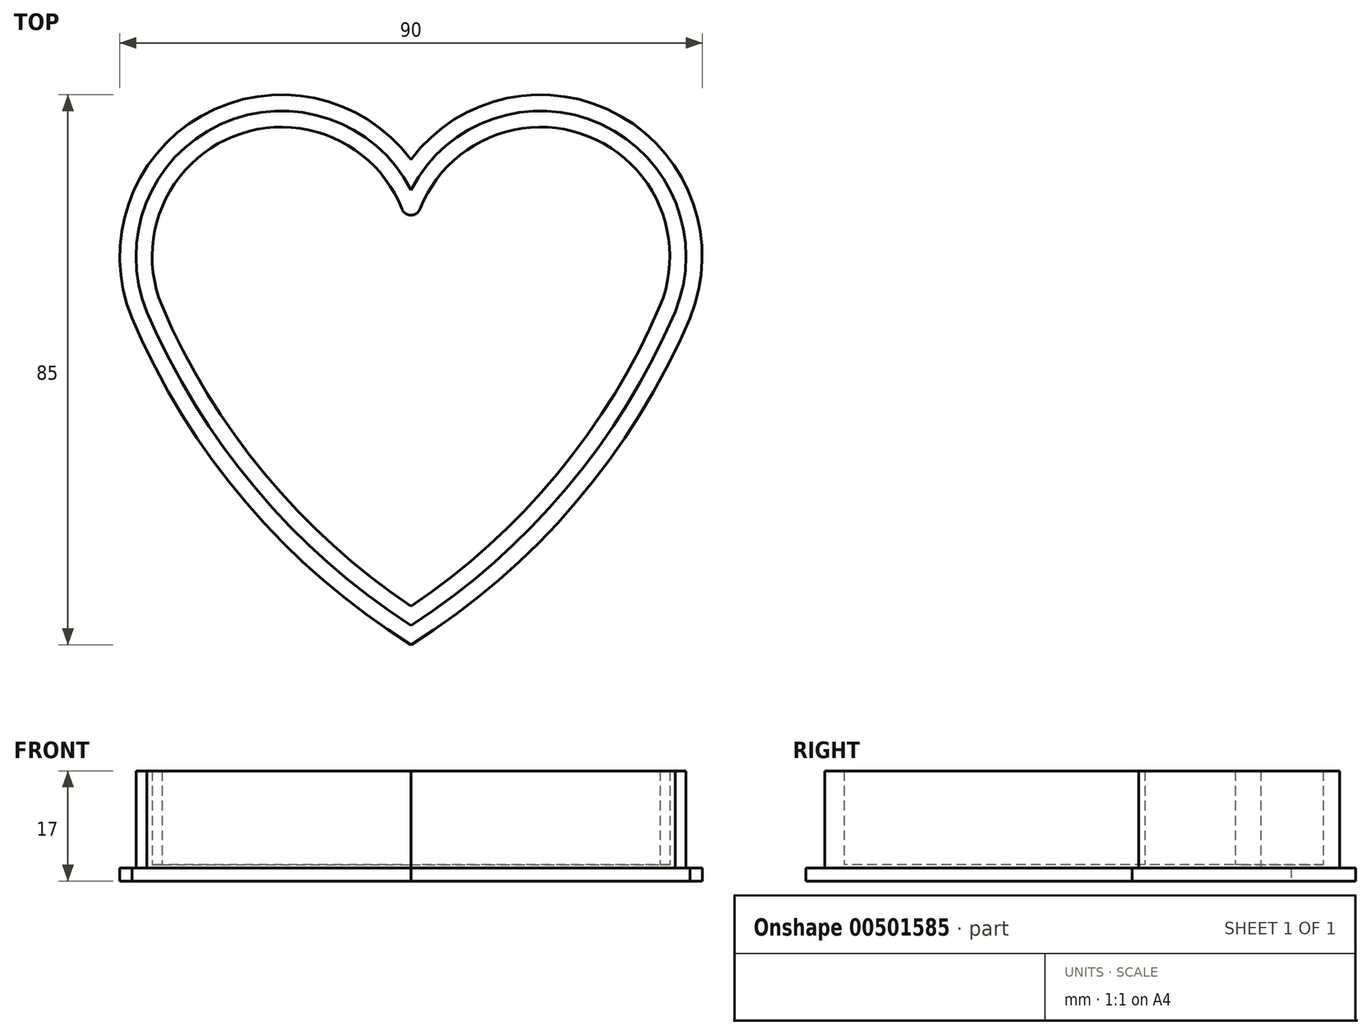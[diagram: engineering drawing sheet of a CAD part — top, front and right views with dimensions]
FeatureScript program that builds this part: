
annotation { "Feature Type Name" : "Feature", "Feature Type Description" : "" }
export const myFeature = defineFeature(function(context is Context, id is Id, definition is map)
    precondition{}
    {
        {
            var Q0;
            Q0=qCreatedBy(makeId("Top.planeOp"),FACE);
            var sketch = newSketch(context, id + "F0", { "sketchPlane" : qUnion([Q0])});
            skArc(sketch, "E0", {"start": v(-43.12, 5.48) * mm, "mid": v(-25.44, -23.07) * mm, "end": v(0, -45) * mm});
            skArc(sketch, "E1", {"start": v(0, 30) * mm, "mid": v(-32.36, 36.73) * mm, "end": v(-43.12, 5.48) * mm});
            skArc(sketch, "E2.MirrorCS", {"start": v(0, 30) * mm, "mid": v(32.36, 36.73) * mm, "end": v(43.12, 5.48) * mm});
            skArc(sketch, "E3.MirrorCS", {"start": v(43.12, 5.48) * mm, "mid": v(25.44, -23.07) * mm, "end": v(0, -45) * mm});
            skPoint(sketch, "E4.orphan", {"position": v(-1.9, 32.24) * mm});
            skPoint(sketch, "E5.orphan", {"position": v(1.9, 32.24) * mm});
            skSolve(sketch);
        }
        {
            var Q0;
            Q0=qSketchRegion(id+"F0",true);
            extrude(context, id + "F1", {"entities" : qUnion([Q0]), "depth" : 2 * mm});
        }
        {
            var Q0;
            Q0=makeQuery(id+"F1.opExtrude","CAP_FACE",FACE,{"disambiguationData":[OSD([sQuery(id+"F0.wireOp",EDGE,"E0"),sQuery(id+"F0.wireOp",EDGE,"E1"),sQuery(id+"F0.wireOp",EDGE,"E2.MirrorCS"),sQuery(id+"F0.wireOp",EDGE,"E3.MirrorCS")])],"isStart":false});
            var sketch = newSketch(context, id + "F2", { "sketchPlane" : qUnion([Q0])});
            skArc(sketch, "E6.0", {"start": v(-40.82, 6.46) * mm, "mid": v(-24.01, -20.82) * mm, "end": v(0, -42.03) * mm});
            skArc(sketch, "E7", {"start": v(0, 25.3) * mm, "mid": v(-29.44, 35.42) * mm, "end": v(-40.81, 6.45) * mm});
            skArc(sketch, "E8.MirrorCS", {"start": v(0, 25.3) * mm, "mid": v(29.44, 35.42) * mm, "end": v(40.81, 6.45) * mm});
            skArc(sketch, "E9.MirrorCS", {"start": v(40.82, 6.46) * mm, "mid": v(24.01, -20.82) * mm, "end": v(0, -42.03) * mm});
            skSolve(sketch);
        }
        {
            var Q0;
            Q0=qSketchRegion(id+"F2",true);
            extrude(context, id + "F3", {"entities" : qUnion([Q0]), "operationType" : NewBodyOperationType.ADD, "depth" : 15 * mm});
        }
        {
            var Q0;
            Q0=makeQuery(id+"F3.opExtrude","CAP_FACE",FACE,{"disambiguationData":[OSD([sQuery(id+"F2.wireOp",EDGE,"E6.0"),sQuery(id+"F2.wireOp",EDGE,"E7"),sQuery(id+"F2.wireOp",EDGE,"E8.MirrorCS"),sQuery(id+"F2.wireOp",EDGE,"E9.MirrorCS")])],"isStart":false});
            shell(context, id + "F4", {"entities" : qUnion([Q0]), "thickness" : 2.5 * mm});
        }
        {
            var Q0;
            Q0=makeQuery(id+"F4.opShell","OFFSET_EDGE",EDGE,{"disambiguationData":[OSD([sQuery(id+"F2.wireOp",EDGE,"E7"),sQuery(id+"F2.wireOp",EDGE,"E8.MirrorCS")])]});
            fillet(context, id + "F5", {"entities" : qUnion([Q0]), "radius" : 1.5 * mm, "tangentPropagation" : true, "allowEdgeOverflow" : false});
        }
    });
